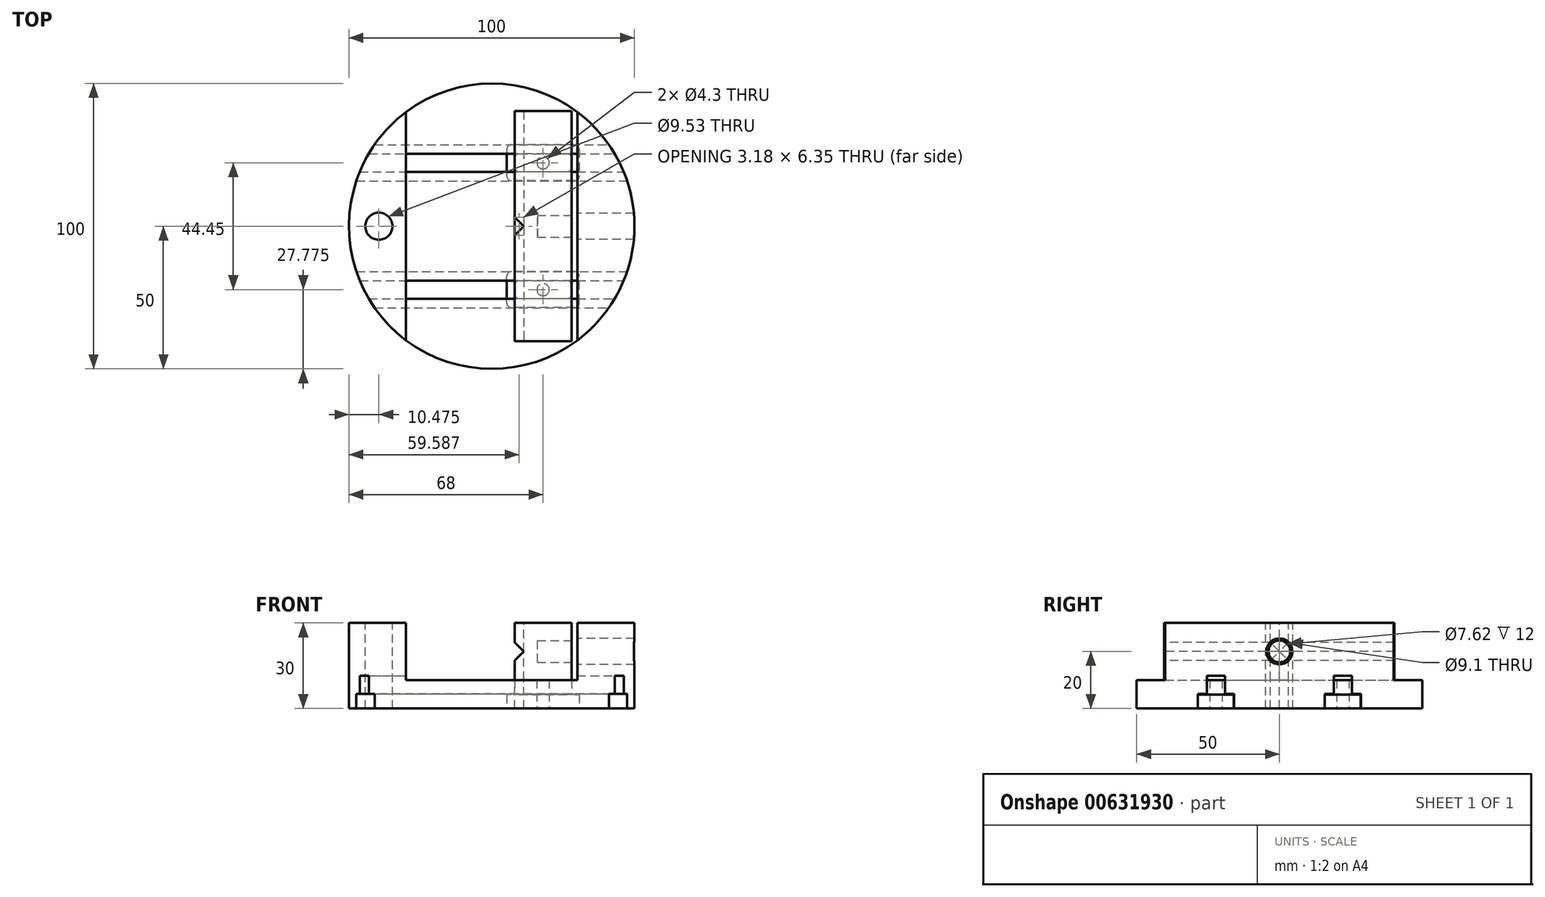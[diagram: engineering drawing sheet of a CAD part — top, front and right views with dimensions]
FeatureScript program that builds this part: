
annotation { "Feature Type Name" : "Feature", "Feature Type Description" : "" }
export const myFeature = defineFeature(function(context is Context, id is Id, definition is map)
    precondition{}
    {
        {
            var Q0;
            Q0=qCreatedBy(makeId("Top.planeOp"),FACE);
            var sketch = newSketch(context, id + "F0", { "sketchPlane" : qUnion([Q0])});
            skCircle(sketch, "E0", {"center": v(0, 0) * mm, "radius": 50 * mm});
            skSolve(sketch);
        }
        {
            var Q0;
            Q0 = qSketchRegion(id + "F0", true);
            extrude(context, id + "F1", {"entities" : qUnion([Q0]), "depth" : 30 * mm, "offsetDistance" : 25.4 * mm});
        }
        {
            var Q0;
            Q0=makeQuery(id+"F1.opExtrude","CAP_FACE",FACE,{"disambiguationData":[OSD([sQuery(id+"F0.wireOp",EDGE,"E0")])],"isStart":false});
            var sketch = newSketch(context, id + "F2", { "sketchPlane" : qUnion([Q0])});
            skLineSegment(sketch, "E1.bottom", {"start": v(30, 52.39) * mm, "end": v(-30, 52.39) * mm});
            skLineSegment(sketch, "E1.top", {"start": v(30, -52.39) * mm, "end": v(-30, -52.39) * mm});
            skLineSegment(sketch, "E1.left", {"start": v(30, 52.39) * mm, "end": v(30, -52.39) * mm});
            skLineSegment(sketch, "E1.right", {"start": v(-30, 52.39) * mm, "end": v(-30, -52.39) * mm});
            skPoint(sketch, "E1.middle", {"position": v(0, 0) * mm});
            skSolve(sketch);
        }
        {
            var Q0;
            Q0 = qSketchRegion(id + "F2", true);
            extrude(context, id + "F3", {"entities" : qUnion([Q0]), "operationType" : NewBodyOperationType.REMOVE, "oppositeDirection" : true, "depth" : 20 * mm, "offsetDistance" : 25.4 * mm});
        }
        {
            var Q0;
            Q0=qCreatedBy(makeId("Right.planeOp"),FACE);
            var sketch = newSketch(context, id + "F4", { "sketchPlane" : qUnion([Q0])});
            skLineSegment(sketch, "E2.bottom", {"start": v(-28.58, 0) * mm, "end": v(-15.88, 0) * mm});
            skLineSegment(sketch, "E2.top", {"start": v(-28.58, 5.08) * mm, "end": v(-15.88, 5.08) * mm});
            skLineSegment(sketch, "E2.left", {"start": v(-28.58, 0) * mm, "end": v(-28.58, 5.08) * mm});
            skLineSegment(sketch, "E2.right", {"start": v(-15.88, 0) * mm, "end": v(-15.88, 5.08) * mm});
            skLineSegment(sketch, "E3.MirrorCS", {"start": v(28.58, 0) * mm, "end": v(15.88, 0) * mm});
            skLineSegment(sketch, "E4.MirrorCS", {"start": v(28.58, 5.08) * mm, "end": v(15.88, 5.08) * mm});
            skLineSegment(sketch, "E5.MirrorCS", {"start": v(15.88, 0) * mm, "end": v(15.88, 5.08) * mm});
            skLineSegment(sketch, "E6.MirrorCS", {"start": v(28.58, 0) * mm, "end": v(28.58, 5.08) * mm});
            skSolve(sketch);
        }
        {
            var Q0;
            Q0 = qSketchRegion(id + "F4", true);
            extrude(context, id + "F5", {"entities" : qUnion([Q0]), "operationType" : NewBodyOperationType.REMOVE, "endBound" : BoundingType.THROUGH_ALL, "oppositeDirection" : true, "depth" : 25.4 * mm, "offsetDistance" : 25.4 * mm, "hasSecondDirection" : true, "secondDirectionBound" : SecondDirectionBoundingType.THROUGH_ALL, "secondDirectionOppositeDirection" : false, "secondDirectionDepth" : 25.4 * mm});
        }
        {
            var Q0;
            Q0=qCreatedBy(makeId("Right.planeOp"),FACE);
            var sketch = newSketch(context, id + "F6", { "sketchPlane" : qUnion([Q0])});
            skLineSegment(sketch, "E7.bottom", {"start": v(-19.05, -1.27) * mm, "end": v(-25.4, -1.27) * mm});
            skLineSegment(sketch, "E7.top", {"start": v(-19.05, 11.43) * mm, "end": v(-25.4, 11.43) * mm});
            skLineSegment(sketch, "E7.left", {"start": v(-19.05, -1.27) * mm, "end": v(-19.05, 11.43) * mm});
            skLineSegment(sketch, "E7.right", {"start": v(-25.4, -1.27) * mm, "end": v(-25.4, 11.43) * mm});
            skPoint(sketch, "E7.middle", {"position": v(-22.23, 5.08) * mm});
            skLineSegment(sketch, "E8.MirrorCS", {"start": v(19.05, -1.27) * mm, "end": v(19.05, 11.43) * mm});
            skLineSegment(sketch, "E9.MirrorCS", {"start": v(25.4, -1.27) * mm, "end": v(25.4, 11.43) * mm});
            skPoint(sketch, "E10.MirrorP", {"position": v(22.23, 5.08) * mm});
            skLineSegment(sketch, "E11.MirrorCS", {"start": v(19.05, 11.43) * mm, "end": v(25.4, 11.43) * mm});
            skLineSegment(sketch, "E12.MirrorCS", {"start": v(19.05, -1.27) * mm, "end": v(25.4, -1.27) * mm});
            skSolve(sketch);
        }
        {
            var Q0;
            Q0 = qSketchRegion(id + "F6", true);
            extrude(context, id + "F7", {"entities" : qUnion([Q0]), "operationType" : NewBodyOperationType.REMOVE, "endBound" : BoundingType.THROUGH_ALL, "oppositeDirection" : true, "depth" : 25.4 * mm, "offsetDistance" : 25.4 * mm, "hasSecondDirection" : true, "secondDirectionBound" : SecondDirectionBoundingType.THROUGH_ALL, "secondDirectionOppositeDirection" : false, "secondDirectionDepth" : 25.4 * mm});
        }
        {
            var Q0;
            Q0=qCreatedBy(makeId("Right.planeOp"),FACE);
            var sketch = newSketch(context, id + "F8", { "sketchPlane" : qUnion([Q0])});
            skCircle(sketch, "E13", {"center": v(0, 20) * mm, "radius": 4.55 * mm});
            skSolve(sketch);
        }
        {
            var Q0;
            Q0 = qSketchRegion(id + "F8", true);
            extrude(context, id + "F9", {"entities" : qUnion([Q0]), "operationType" : NewBodyOperationType.REMOVE, "endBound" : BoundingType.THROUGH_ALL, "depth" : 25.4 * mm, "offsetDistance" : 25.4 * mm});
        }
        {
            var Q0;
            {var subQ0=sQuery(id+"F0.wireOp",EDGE,"E0");Q0=makeQuery(id+"F5.boolean.opBoolean","SPLIT",FACE,{"disambiguationData":[TD([makeQuery(id+"F5.opExtrude","SWEPT_FACE",FACE,{"disambiguationData":[OSD([sQuery(id+"F4.wireOp",EDGE,"E2.right")])]})])],"derivedFrom":makeQuery(id+"F1.opExtrude","CAP_FACE",FACE,{"disambiguationData":[OSD([subQ0])],"isStart":true})});}
            var sketch = newSketch(context, id + "F10", { "sketchPlane" : qUnion([Q0])});
            skLineSegment(sketch, "E14.bottom", {"start": v(29.11, -28.5) * mm, "end": v(6.89, -28.5) * mm});
            skLineSegment(sketch, "E14.top", {"start": v(29.11, -15.95) * mm, "end": v(6.89, -15.95) * mm});
            skLineSegment(sketch, "E14.left", {"start": v(30.7, -26.91) * mm, "end": v(30.7, -17.54) * mm});
            skLineSegment(sketch, "E14.right", {"start": v(5.3, -26.91) * mm, "end": v(5.3, -17.54) * mm});
            skPoint(sketch, "E14.middle", {"position": v(18, -22.23) * mm});
            skCircle(sketch, "E15", {"center": v(18, -22.23) * mm, "radius": 2.15 * mm});
            skPoint(sketch, "E16.visualSharp", {"position": v(30.7, -15.95) * mm});
            skArc(sketch, "E16.filletArc", {"start": v(30.7, -17.54) * mm, "mid": v(30.24, -16.42) * mm, "end": v(29.11, -15.95) * mm});
            skPoint(sketch, "E17.visualSharp", {"position": v(30.7, -28.5) * mm});
            skArc(sketch, "E17.filletArc", {"start": v(29.11, -28.5) * mm, "mid": v(30.24, -28.03) * mm, "end": v(30.7, -26.91) * mm});
            skPoint(sketch, "E18.visualSharp", {"position": v(5.3, -28.5) * mm});
            skArc(sketch, "E18.filletArc", {"start": v(5.3, -26.91) * mm, "mid": v(5.76, -28.03) * mm, "end": v(6.89, -28.5) * mm});
            skPoint(sketch, "E19.visualSharp", {"position": v(5.3, -15.95) * mm});
            skArc(sketch, "E19.filletArc", {"start": v(6.89, -15.95) * mm, "mid": v(5.76, -16.42) * mm, "end": v(5.3, -17.54) * mm});
            skSolve(sketch);
        }
        {
            var Q0;
            Q0=makeQuery(id+"F10.imprint","IMPRINT",FACE,{"disambiguationData":[TD([[makeQuery(id+"F10.imprint","IMPRINT",EDGE,{"derivedFrom":sQuery(id+"F10.wireOp",EDGE,"E14.bottom")}),-1.0]])]});
            extrude(context, id + "F11", {"entities" : qUnion([Q0]), "oppositeDirection" : true, "depth" : 4.83 * mm, "offsetDistance" : 25.4 * mm});
        }
        {
            var Q0;
            Q0=makeQuery(id+"F11.opExtrude","CAP_FACE",FACE,{"disambiguationData":[OSD([sQuery(id+"F10.wireOp",EDGE,"E14.bottom"),sQuery(id+"F10.wireOp",EDGE,"E14.top"),sQuery(id+"F10.wireOp",EDGE,"E14.left"),sQuery(id+"F10.wireOp",EDGE,"E14.right"),sQuery(id+"F10.wireOp",EDGE,"E15"),sQuery(id+"F10.wireOp",EDGE,"E16.filletArc"),sQuery(id+"F10.wireOp",EDGE,"E17.filletArc"),sQuery(id+"F10.wireOp",EDGE,"E18.filletArc"),sQuery(id+"F10.wireOp",EDGE,"E19.filletArc")])],"isStart":false});
            var sketch = newSketch(context, id + "F12", { "sketchPlane" : qUnion([Q0])});
            skLineSegment(sketch, "E20.bottom", {"start": v(9.59, 19.1) * mm, "end": v(26.41, 19.1) * mm});
            skLineSegment(sketch, "E20.top", {"start": v(9.59, 25.35) * mm, "end": v(26.41, 25.35) * mm});
            skLineSegment(sketch, "E20.left", {"start": v(8, 20.69) * mm, "end": v(8, 23.76) * mm});
            skLineSegment(sketch, "E20.right", {"start": v(28, 20.69) * mm, "end": v(28, 23.76) * mm});
            skPoint(sketch, "E20.middle", {"position": v(18, 22.23) * mm});
            skPoint(sketch, "E21.visualSharp", {"position": v(8, 25.35) * mm});
            skArc(sketch, "E21.filletArc", {"start": v(9.59, 25.35) * mm, "mid": v(8.46, 24.88) * mm, "end": v(8, 23.76) * mm});
            skPoint(sketch, "E22.visualSharp", {"position": v(28, 25.35) * mm});
            skArc(sketch, "E22.filletArc", {"start": v(28, 23.76) * mm, "mid": v(27.54, 24.88) * mm, "end": v(26.41, 25.35) * mm});
            skPoint(sketch, "E23.visualSharp", {"position": v(28, 19.1) * mm});
            skArc(sketch, "E23.filletArc", {"start": v(26.41, 19.1) * mm, "mid": v(27.54, 19.57) * mm, "end": v(28, 20.69) * mm});
            skPoint(sketch, "E24.visualSharp", {"position": v(8, 19.1) * mm});
            skArc(sketch, "E24.filletArc", {"start": v(8, 20.69) * mm, "mid": v(8.46, 19.57) * mm, "end": v(9.59, 19.1) * mm});
            skCircle(sketch, "E25.0", {"center": v(18, 22.23) * mm, "radius": 2.15 * mm});
            skSolve(sketch);
        }
        {
            var Q0;
            Q0 = qSketchRegion(id + "F12", true);
            var Q1;
            {var subQ0=sQuery(id+"F2.wireOp",EDGE,"E1.left");var subQ1=sQuery(id+"F2.wireOp",EDGE,"E1.right");Q1=makeQuery(id+"F7.boolean.opBoolean","SPLIT",FACE,{"disambiguationData":[TD([makeQuery(id+"F7.opExtrude","SWEPT_FACE",FACE,{"disambiguationData":[OSD([sQuery(id+"F6.wireOp",EDGE,"E7.left")])]})])],"derivedFrom":makeQuery(id+"F3.boolean.opBoolean","COPY",FACE,{"derivedFrom":makeQuery(id+"F3.opExtrude","CAP_FACE",FACE,{"disambiguationData":[OSD([sQuery(id+"F2.wireOp",EDGE,"E1.bottom"),sQuery(id+"F2.wireOp",EDGE,"E1.top"),subQ0,subQ1])],"isStart":false})})});}
            extrude(context, id + "F13", {"entities" : qUnion([Q0]), "operationType" : NewBodyOperationType.ADD, "endBound" : BoundingType.UP_TO_SURFACE, "depth" : 25.4 * mm, "endBoundEntityFace" : qUnion([Q1]), "offsetDistance" : 25.4 * mm});
        }
        {
            var Q0;
            Q0=makeQuery(id+"F11.opExtrude","SWEPT_BODY",BODY,{"disambiguationData":[OSD([sQuery(id+"F10.wireOp",EDGE,"E14.bottom"),sQuery(id+"F10.wireOp",EDGE,"E14.top"),sQuery(id+"F10.wireOp",EDGE,"E14.left"),sQuery(id+"F10.wireOp",EDGE,"E14.right"),sQuery(id+"F10.wireOp",EDGE,"E15"),sQuery(id+"F10.wireOp",EDGE,"E16.filletArc"),sQuery(id+"F10.wireOp",EDGE,"E17.filletArc"),sQuery(id+"F10.wireOp",EDGE,"E18.filletArc"),sQuery(id+"F10.wireOp",EDGE,"E19.filletArc")])]});
            var Q1;
            Q1=qCreatedBy(makeId("Front.planeOp"),FACE);
            mirror(context, id + "F14", {"entities" : qUnion([Q0]), "mirrorPlane" : qUnion([Q1])});
        }
        {
            var Q0;
            Q0=qCreatedBy(makeId("Front.planeOp"),FACE);
            var sketch = newSketch(context, id + "F15", { "sketchPlane" : qUnion([Q0])});
            skLineSegment(sketch, "E26.bottom", {"start": v(8, 10) * mm, "end": v(28, 10) * mm});
            skLineSegment(sketch, "E26.top", {"start": v(8, 30) * mm, "end": v(28, 30) * mm});
            skLineSegment(sketch, "E26.left", {"start": v(8, 10) * mm, "end": v(8, 30) * mm});
            skLineSegment(sketch, "E26.right", {"start": v(28, 10) * mm, "end": v(28, 30) * mm});
            skPoint(sketch, "E26.middle", {"position": v(18, 20) * mm});
            skSolve(sketch);
        }
        {
            var Q0;
            Q0=makeQuery(id+"F15.imprint","IMPRINT",FACE,{"disambiguationData":[TD([[makeQuery(id+"F15.imprint","IMPRINT",EDGE,{"derivedFrom":sQuery(id+"F15.wireOp",EDGE,"E26.bottom")}),1.0]])]});
            extrude(context, id + "F16", {"entities" : qUnion([Q0]), "endBound" : BoundingType.SYMMETRIC, "depth" : 80.64 * mm, "offsetDistance" : 25.4 * mm});
        }
        {
            var Q0;
            Q0=makeQuery(id+"F16.opExtrude","SWEPT_FACE",FACE,{"disambiguationData":[OSD([sQuery(id+"F15.wireOp",EDGE,"E26.right")])]});
            var sketch = newSketch(context, id + "F17", { "sketchPlane" : qUnion([Q0])});
            skCircle(sketch, "E27.0", {"center": v(0, 20) * mm, "radius": 4.55 * mm, "construction": true});
            skCircle(sketch, "E28", {"center": v(0, 20) * mm, "radius": 3.81 * mm});
            skSolve(sketch);
        }
        {
            var Q0;
            Q0=makeQuery(id+"F17.imprint","IMPRINT",FACE,{"disambiguationData":[TD([[makeQuery(id+"F17.imprint","IMPRINT",EDGE,{"derivedFrom":sQuery(id+"F17.wireOp",EDGE,"E28")}),1.0]])]});
            extrude(context, id + "F18", {"entities" : qUnion([Q0]), "operationType" : NewBodyOperationType.REMOVE, "oppositeDirection" : true, "depth" : 12 * mm, "offsetDistance" : 25.4 * mm});
        }
        {
            var Q0;
            Q0=makeQuery(id+"F16.opExtrude","CAP_FACE",FACE,{"disambiguationData":[OSD([sQuery(id+"F15.wireOp",EDGE,"E26.bottom"),sQuery(id+"F15.wireOp",EDGE,"E26.top"),sQuery(id+"F15.wireOp",EDGE,"E26.left"),sQuery(id+"F15.wireOp",EDGE,"E26.right")])],"isStart":false});
            var sketch = newSketch(context, id + "F19", { "sketchPlane" : qUnion([Q0])});
            skLineSegment(sketch, "E29", {"start": v(2.7, 20) * mm, "end": v(2.7, 11.53) * mm});
            skLineSegment(sketch, "E30", {"start": v(2.7, 11.53) * mm, "end": v(11.18, 20) * mm});
            skLineSegment(sketch, "E31", {"start": v(11.18, 20) * mm, "end": v(2.7, 28.47) * mm});
            skLineSegment(sketch, "E32", {"start": v(2.7, 28.47) * mm, "end": v(2.7, 20) * mm});
            skSolve(sketch);
        }
        {
            var Q0;
            {var subQ0=sQuery(id+"F19.wireOp",EDGE,"E31");var subQ1=sQuery(id+"F19.wireOp",EDGE,"E30");var subQ2=makeQuery(id+"F19.imprint","INTERSECT",VERTEX,{"derivedFrom":[subQ1,subQ0]});Q0=makeQuery(id+"F19.imprint","IMPRINT",FACE,{"disambiguationData":[TD([[makeQuery(id+"F19.imprint","IMPRINT",EDGE,{"disambiguationData":[TD([[subQ2,1.0]])],"derivedFrom":subQ1}),1.0]])]});}
            extrude(context, id + "F20", {"entities" : qUnion([Q0]), "operationType" : NewBodyOperationType.REMOVE, "endBound" : BoundingType.THROUGH_ALL, "oppositeDirection" : true, "depth" : 25.4 * mm, "offsetDistance" : 25.4 * mm});
        }
        {
            var Q0;
            Q0=makeQuery(id+"F16.opExtrude","SWEPT_FACE",FACE,{"disambiguationData":[OSD([sQuery(id+"F15.wireOp",EDGE,"E26.top")])]});
            var sketch = newSketch(context, id + "F21", { "sketchPlane" : qUnion([Q0])});
            skLineSegment(sketch, "E33", {"start": v(4.4, 0) * mm, "end": v(4.4, 6.78) * mm});
            skLineSegment(sketch, "E34", {"start": v(4.4, 6.78) * mm, "end": v(11.18, 0) * mm});
            skLineSegment(sketch, "E35", {"start": v(11.18, 0) * mm, "end": v(4.4, -6.78) * mm});
            skLineSegment(sketch, "E36", {"start": v(4.4, -6.78) * mm, "end": v(4.4, 0) * mm});
            skSolve(sketch);
        }
        {
            var Q0;
            {var subQ0=sQuery(id+"F21.wireOp",EDGE,"E35");var subQ1=sQuery(id+"F21.wireOp",EDGE,"E34");var subQ2=makeQuery(id+"F21.imprint","INTERSECT",VERTEX,{"derivedFrom":[subQ1,subQ0]});Q0=makeQuery(id+"F21.imprint","IMPRINT",FACE,{"disambiguationData":[TD([[makeQuery(id+"F21.imprint","IMPRINT",EDGE,{"disambiguationData":[TD([[subQ2,1.0]])],"derivedFrom":subQ1}),-1.0]])]});}
            extrude(context, id + "F22", {"entities" : qUnion([Q0]), "operationType" : NewBodyOperationType.REMOVE, "endBound" : BoundingType.THROUGH_ALL, "oppositeDirection" : true, "depth" : 25.4 * mm, "offsetDistance" : 25.4 * mm});
        }
        {
            var Q0;
            {var subQ0=sQuery(id+"F0.wireOp",EDGE,"E0");Q0=makeQuery(id+"F3.boolean.opBoolean","SPLIT",FACE,{"disambiguationData":[TD([makeQuery(id+"F3.opExtrude","SWEPT_FACE",FACE,{"disambiguationData":[OSD([sQuery(id+"F2.wireOp",EDGE,"E1.right")])]})])],"derivedFrom":makeQuery(id+"F1.opExtrude","CAP_FACE",FACE,{"disambiguationData":[OSD([subQ0])],"isStart":false})});}
            var sketch = newSketch(context, id + "F23", { "sketchPlane" : qUnion([Q0])});
            skCircle(sketch, "E37", {"center": v(-39.53, 0) * mm, "radius": 4.76 * mm});
            skSolve(sketch);
        }
        {
            var Q0;
            Q0 = qSketchRegion(id + "F23", true);
            extrude(context, id + "F24", {"entities" : qUnion([Q0]), "operationType" : NewBodyOperationType.REMOVE, "endBound" : BoundingType.THROUGH_ALL, "oppositeDirection" : true, "depth" : 25.4 * mm, "offsetDistance" : 25.4 * mm});
        }
    });
